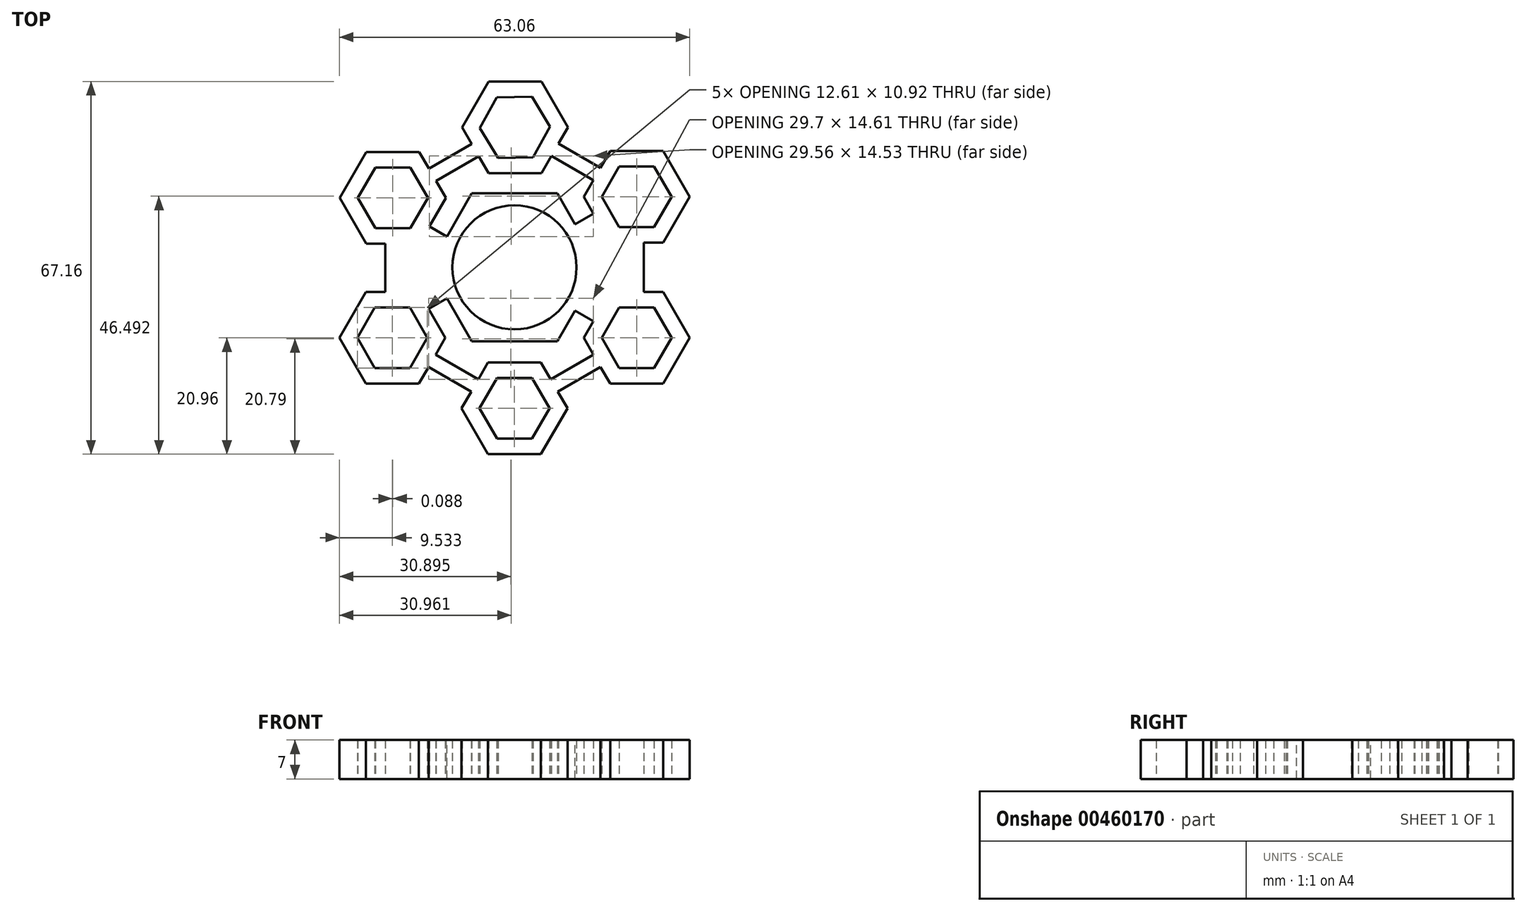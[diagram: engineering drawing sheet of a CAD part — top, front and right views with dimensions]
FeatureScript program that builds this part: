
annotation { "Feature Type Name" : "Feature", "Feature Type Description" : "" }
export const myFeature = defineFeature(function(context is Context, id is Id, definition is map)
    precondition{}
    {
        {
            var Q0;
            Q0=qCreatedBy(makeId("Top.planeOp"),FACE);
            var sketch = newSketch(context, id + "F0", { "sketchPlane" : qUnion([Q0])});
            skCircle(sketch, "E0", {"center": v(0, 0) * mm, "radius": 10.95 * mm});
            skCircle(sketch, "E1.cCircle", {"center": v(0, 0) * mm, "radius": 12.7 * mm, "construction": true});
            skLineSegment(sketch, "E1.0", {"start": v(-7.33, 12.7) * mm, "end": v(7.33, 12.7) * mm});
            skLineSegment(sketch, "E1.1", {"start": v(7.33, 12.7) * mm, "end": v(14.66, 0) * mm});
            skLineSegment(sketch, "E1.2", {"start": v(14.66, 0) * mm, "end": v(7.33, -12.7) * mm});
            skLineSegment(sketch, "E1.3", {"start": v(7.33, -12.7) * mm, "end": v(-7.33, -12.7) * mm});
            skLineSegment(sketch, "E1.4", {"start": v(-7.33, -12.7) * mm, "end": v(-14.66, 0) * mm});
            skLineSegment(sketch, "E1.5", {"start": v(-14.66, 0) * mm, "end": v(-7.33, 12.7) * mm});
            skPoint(sketch, "E1.0.midPoint", {"position": v(0, 12.7) * mm});
            skPoint(sketch, "E2.endSnap0", {"position": v(0, -12.7) * mm});
            skCircle(sketch, "E3.cCircle", {"center": v(0.09, 25.25) * mm, "radius": 5.46 * mm, "construction": true});
            skLineSegment(sketch, "E3.0", {"start": v(3.36, 19.86) * mm, "end": v(-2.94, 19.72) * mm});
            skLineSegment(sketch, "E3.1", {"start": v(-2.94, 19.72) * mm, "end": v(-6.22, 25.1) * mm});
            skLineSegment(sketch, "E3.2", {"start": v(-6.22, 25.1) * mm, "end": v(-3.18, 30.64) * mm});
            skLineSegment(sketch, "E3.3", {"start": v(-3.18, 30.64) * mm, "end": v(3.12, 30.78) * mm});
            skLineSegment(sketch, "E3.4", {"start": v(3.12, 30.78) * mm, "end": v(6.4, 25.39) * mm});
            skLineSegment(sketch, "E3.5", {"start": v(6.4, 25.39) * mm, "end": v(3.36, 19.86) * mm});
            skPoint(sketch, "E3.0.midPoint", {"position": v(0.2, 19.79) * mm});
            skCircle(sketch, "E4.cCircle", {"center": v(22, 12.7) * mm, "radius": 5.46 * mm, "construction": true});
            skLineSegment(sketch, "E4.0", {"start": v(18.84, 7.24) * mm, "end": v(15.7, 12.7) * mm});
            skLineSegment(sketch, "E4.1", {"start": v(15.7, 12.7) * mm, "end": v(18.84, 18.16) * mm});
            skLineSegment(sketch, "E4.2", {"start": v(18.84, 18.16) * mm, "end": v(25.15, 18.16) * mm});
            skLineSegment(sketch, "E4.3", {"start": v(25.15, 18.16) * mm, "end": v(28.3, 12.7) * mm});
            skLineSegment(sketch, "E4.4", {"start": v(28.3, 12.7) * mm, "end": v(25.15, 7.24) * mm});
            skLineSegment(sketch, "E4.5", {"start": v(25.15, 7.24) * mm, "end": v(18.84, 7.24) * mm});
            skPoint(sketch, "E4.0.midPoint", {"position": v(17.27, 9.97) * mm});
            skCircle(sketch, "E5.cCircle", {"center": v(22, -12.7) * mm, "radius": 5.46 * mm, "construction": true});
            skLineSegment(sketch, "E5.0", {"start": v(15.7, -12.7) * mm, "end": v(18.84, -7.24) * mm});
            skLineSegment(sketch, "E5.1", {"start": v(18.84, -7.24) * mm, "end": v(25.15, -7.24) * mm});
            skLineSegment(sketch, "E5.2", {"start": v(25.15, -7.24) * mm, "end": v(28.3, -12.7) * mm});
            skLineSegment(sketch, "E5.3", {"start": v(28.3, -12.7) * mm, "end": v(25.15, -18.16) * mm});
            skLineSegment(sketch, "E5.4", {"start": v(25.15, -18.16) * mm, "end": v(18.84, -18.16) * mm});
            skLineSegment(sketch, "E5.5", {"start": v(18.84, -18.16) * mm, "end": v(15.7, -12.7) * mm});
            skPoint(sketch, "E5.0.midPoint", {"position": v(17.27, -9.97) * mm});
            skCircle(sketch, "E6.cCircle", {"center": v(0, -25.4) * mm, "radius": 5.46 * mm, "construction": true});
            skLineSegment(sketch, "E6.0", {"start": v(-3.15, -19.94) * mm, "end": v(3.15, -19.94) * mm});
            skLineSegment(sketch, "E6.1", {"start": v(3.15, -19.94) * mm, "end": v(6.3, -25.4) * mm});
            skLineSegment(sketch, "E6.2", {"start": v(6.3, -25.4) * mm, "end": v(3.15, -30.86) * mm});
            skLineSegment(sketch, "E6.3", {"start": v(3.15, -30.86) * mm, "end": v(-3.15, -30.86) * mm});
            skLineSegment(sketch, "E6.4", {"start": v(-3.15, -30.86) * mm, "end": v(-6.3, -25.4) * mm});
            skLineSegment(sketch, "E6.5", {"start": v(-6.3, -25.4) * mm, "end": v(-3.15, -19.94) * mm});
            skPoint(sketch, "E6.0.midPoint", {"position": v(0, -19.94) * mm});
            skCircle(sketch, "E7.cCircle", {"center": v(-22, -12.7) * mm, "radius": 5.46 * mm, "construction": true});
            skLineSegment(sketch, "E7.0", {"start": v(-18.84, -7.24) * mm, "end": v(-15.7, -12.7) * mm});
            skLineSegment(sketch, "E7.1", {"start": v(-15.7, -12.7) * mm, "end": v(-18.84, -18.16) * mm});
            skLineSegment(sketch, "E7.2", {"start": v(-18.84, -18.16) * mm, "end": v(-25.15, -18.16) * mm});
            skLineSegment(sketch, "E7.3", {"start": v(-25.15, -18.16) * mm, "end": v(-28.3, -12.7) * mm});
            skLineSegment(sketch, "E7.4", {"start": v(-28.3, -12.7) * mm, "end": v(-25.15, -7.24) * mm});
            skLineSegment(sketch, "E7.5", {"start": v(-25.15, -7.24) * mm, "end": v(-18.84, -7.24) * mm});
            skPoint(sketch, "E7.0.midPoint", {"position": v(-17.27, -9.97) * mm});
            skCircle(sketch, "E8.cCircle", {"center": v(-21.9, 12.55) * mm, "radius": 5.46 * mm, "construction": true});
            skLineSegment(sketch, "E8.0", {"start": v(-15.6, 12.55) * mm, "end": v(-18.76, 7.09) * mm});
            skLineSegment(sketch, "E8.1", {"start": v(-18.76, 7.09) * mm, "end": v(-25.06, 7.09) * mm});
            skLineSegment(sketch, "E8.2", {"start": v(-25.06, 7.09) * mm, "end": v(-28.21, 12.55) * mm});
            skLineSegment(sketch, "E8.3", {"start": v(-28.21, 12.55) * mm, "end": v(-25.06, 18) * mm});
            skLineSegment(sketch, "E8.4", {"start": v(-25.06, 18) * mm, "end": v(-18.76, 18) * mm});
            skLineSegment(sketch, "E8.5", {"start": v(-18.76, 18) * mm, "end": v(-15.6, 12.55) * mm});
            skPoint(sketch, "E8.0.midPoint", {"position": v(-17.18, 9.82) * mm});
            skCircle(sketch, "E9.cCircle", {"center": v(-21.9, 12.55) * mm, "radius": 8.26 * mm, "construction": true});
            skLineSegment(sketch, "E9.0", {"start": v(-12.38, 12.55) * mm, "end": v(-17.14, 4.3) * mm});
            skLineSegment(sketch, "E9.1", {"start": v(-17.14, 4.3) * mm, "end": v(-26.67, 4.3) * mm});
            skLineSegment(sketch, "E9.2", {"start": v(-26.67, 4.3) * mm, "end": v(-31.44, 12.55) * mm});
            skLineSegment(sketch, "E9.3", {"start": v(-31.44, 12.55) * mm, "end": v(-26.67, 20.8) * mm});
            skLineSegment(sketch, "E9.4", {"start": v(-26.67, 20.8) * mm, "end": v(-17.14, 20.8) * mm});
            skLineSegment(sketch, "E9.5", {"start": v(-17.14, 20.8) * mm, "end": v(-12.38, 12.55) * mm});
            skPoint(sketch, "E9.0.midPoint", {"position": v(-14.76, 8.42) * mm});
            skCircle(sketch, "E10.cCircle", {"center": v(0.09, 25.25) * mm, "radius": 8.26 * mm, "construction": true});
            skLineSegment(sketch, "E10.0", {"start": v(4.85, 17) * mm, "end": v(-4.68, 17) * mm});
            skLineSegment(sketch, "E10.1", {"start": v(-4.68, 17) * mm, "end": v(-9.44, 25.25) * mm});
            skLineSegment(sketch, "E10.2", {"start": v(-9.44, 25.25) * mm, "end": v(-4.68, 33.5) * mm});
            skLineSegment(sketch, "E10.3", {"start": v(-4.68, 33.5) * mm, "end": v(4.85, 33.5) * mm});
            skLineSegment(sketch, "E10.4", {"start": v(4.85, 33.5) * mm, "end": v(9.62, 25.25) * mm});
            skLineSegment(sketch, "E10.5", {"start": v(9.62, 25.25) * mm, "end": v(4.85, 17) * mm});
            skPoint(sketch, "E10.0.midPoint", {"position": v(0.09, 17) * mm});
            skCircle(sketch, "E11.cCircle", {"center": v(22, 12.7) * mm, "radius": 8.26 * mm, "construction": true});
            skLineSegment(sketch, "E11.0", {"start": v(17.23, 4.45) * mm, "end": v(12.46, 12.7) * mm});
            skLineSegment(sketch, "E11.1", {"start": v(12.46, 12.7) * mm, "end": v(17.23, 20.96) * mm});
            skLineSegment(sketch, "E11.2", {"start": v(17.23, 20.96) * mm, "end": v(26.76, 20.96) * mm});
            skLineSegment(sketch, "E11.3", {"start": v(26.76, 20.96) * mm, "end": v(31.53, 12.7) * mm});
            skLineSegment(sketch, "E11.4", {"start": v(31.53, 12.7) * mm, "end": v(26.76, 4.45) * mm});
            skLineSegment(sketch, "E11.5", {"start": v(26.76, 4.45) * mm, "end": v(17.23, 4.45) * mm});
            skPoint(sketch, "E11.0.midPoint", {"position": v(14.85, 8.57) * mm});
            skCircle(sketch, "E12.cCircle", {"center": v(22, -12.7) * mm, "radius": 8.26 * mm, "construction": true});
            skLineSegment(sketch, "E12.0", {"start": v(12.46, -12.7) * mm, "end": v(17.23, -4.44) * mm});
            skLineSegment(sketch, "E12.1", {"start": v(17.23, -4.45) * mm, "end": v(26.76, -4.44) * mm});
            skLineSegment(sketch, "E12.2", {"start": v(26.76, -4.44) * mm, "end": v(31.53, -12.7) * mm});
            skLineSegment(sketch, "E12.3", {"start": v(31.53, -12.7) * mm, "end": v(26.76, -20.96) * mm});
            skLineSegment(sketch, "E12.4", {"start": v(26.76, -20.96) * mm, "end": v(17.23, -20.96) * mm});
            skLineSegment(sketch, "E12.5", {"start": v(17.23, -20.96) * mm, "end": v(12.46, -12.7) * mm});
            skPoint(sketch, "E12.0.midPoint", {"position": v(14.85, -8.57) * mm});
            skCircle(sketch, "E13.cCircle", {"center": v(0, -25.4) * mm, "radius": 8.26 * mm, "construction": true});
            skLineSegment(sketch, "E13.0", {"start": v(-4.77, -17.14) * mm, "end": v(4.77, -17.14) * mm});
            skLineSegment(sketch, "E13.1", {"start": v(4.77, -17.15) * mm, "end": v(9.53, -25.4) * mm});
            skLineSegment(sketch, "E13.2", {"start": v(9.53, -25.4) * mm, "end": v(4.77, -33.65) * mm});
            skLineSegment(sketch, "E13.3", {"start": v(4.77, -33.65) * mm, "end": v(-4.77, -33.66) * mm});
            skLineSegment(sketch, "E13.4", {"start": v(-4.77, -33.66) * mm, "end": v(-9.53, -25.4) * mm});
            skLineSegment(sketch, "E13.5", {"start": v(-9.53, -25.4) * mm, "end": v(-4.77, -17.15) * mm});
            skPoint(sketch, "E13.0.midPoint", {"position": v(0, -17.14) * mm});
            skCircle(sketch, "E14.cCircle", {"center": v(-22, -12.7) * mm, "radius": 8.26 * mm, "construction": true});
            skLineSegment(sketch, "E14.0", {"start": v(-17.23, -4.45) * mm, "end": v(-12.46, -12.7) * mm});
            skLineSegment(sketch, "E14.1", {"start": v(-12.46, -12.7) * mm, "end": v(-17.23, -20.96) * mm});
            skLineSegment(sketch, "E14.2", {"start": v(-17.23, -20.96) * mm, "end": v(-26.76, -20.96) * mm});
            skLineSegment(sketch, "E14.3", {"start": v(-26.76, -20.96) * mm, "end": v(-31.53, -12.7) * mm});
            skLineSegment(sketch, "E14.4", {"start": v(-31.53, -12.7) * mm, "end": v(-26.76, -4.45) * mm});
            skLineSegment(sketch, "E14.5", {"start": v(-26.76, -4.45) * mm, "end": v(-17.23, -4.45) * mm});
            skPoint(sketch, "E14.0.midPoint", {"position": v(-14.85, -8.57) * mm});
            skLineSegment(sketch, "E15", {"start": v(-6.43, 20.02) * mm, "end": v(-14.12, 15.57) * mm});
            skLineSegment(sketch, "E16", {"start": v(-14.21, 15.73) * mm, "end": v(-15.4, 17.77) * mm});
            skLineSegment(sketch, "E17", {"start": v(-15.4, 17.77) * mm, "end": v(-7.7, 22.22) * mm});
            skLineSegment(sketch, "E18", {"start": v(-23.27, 4.3) * mm, "end": v(-23.27, -4.45) * mm});
            skLineSegment(sketch, "E19", {"start": v(-23.27, -4.45) * mm, "end": v(-20.73, -4.45) * mm});
            skLineSegment(sketch, "E20", {"start": v(-20.73, -4.45) * mm, "end": v(-20.73, 4.3) * mm});
            skLineSegment(sketch, "E21", {"start": v(-15.48, -17.93) * mm, "end": v(-7.78, -22.37) * mm});
            skLineSegment(sketch, "E22", {"start": v(-7.78, -22.37) * mm, "end": v(-6.51, -20.17) * mm});
            skLineSegment(sketch, "E23", {"start": v(-6.51, -20.17) * mm, "end": v(-14.21, -15.73) * mm});
            skLineSegment(sketch, "E24", {"start": v(6.51, -20.17) * mm, "end": v(14.21, -15.73) * mm});
            skLineSegment(sketch, "E25", {"start": v(14.21, -15.73) * mm, "end": v(15.48, -17.93) * mm});
            skLineSegment(sketch, "E26", {"start": v(15.48, -17.93) * mm, "end": v(7.7, -22.42) * mm});
            skLineSegment(sketch, "E27", {"start": v(20.73, -4.45) * mm, "end": v(20.73, 4.45) * mm});
            skLineSegment(sketch, "E28", {"start": v(20.73, 4.45) * mm, "end": v(23.27, 4.45) * mm});
            skLineSegment(sketch, "E29", {"start": v(23.27, 4.45) * mm, "end": v(23.27, -4.54) * mm});
            skLineSegment(sketch, "E30", {"start": v(14.21, 15.73) * mm, "end": v(6.65, 20.1) * mm});
            skLineSegment(sketch, "E31", {"start": v(6.65, 20.1) * mm, "end": v(7.92, 22.3) * mm});
            skLineSegment(sketch, "E32", {"start": v(7.92, 22.3) * mm, "end": v(15.48, 17.93) * mm});
            skLineSegment(sketch, "E33.bottom", {"start": v(-1.27, -12.7) * mm, "end": v(1.27, -12.7) * mm});
            skLineSegment(sketch, "E33.top", {"start": v(-1.27, -17.14) * mm, "end": v(1.27, -17.14) * mm});
            skLineSegment(sketch, "E34.bottom", {"start": v(1.27, 12.7) * mm, "end": v(-1.27, 12.7) * mm});
            skLineSegment(sketch, "E34.top", {"start": v(1.27, 17) * mm, "end": v(-1.27, 17) * mm});
            skLineSegment(sketch, "E35", {"start": v(14.21, 9.67) * mm, "end": v(10.3, 7.42) * mm});
            skLineSegment(sketch, "E36", {"start": v(10.3, 7.42) * mm, "end": v(11.63, 5.25) * mm});
            skLineSegment(sketch, "E37", {"start": v(11.63, 5.25) * mm, "end": v(15.48, 7.47) * mm});
            skLineSegment(sketch, "E38", {"start": v(15.48, -7.47) * mm, "end": v(11.58, -5.22) * mm});
            skLineSegment(sketch, "E39", {"start": v(11.58, -5.22) * mm, "end": v(10.36, -7.45) * mm});
            skLineSegment(sketch, "E40", {"start": v(10.36, -7.45) * mm, "end": v(14.21, -9.67) * mm});
            skLineSegment(sketch, "E41", {"start": v(-10.36, -7.45) * mm, "end": v(-14.21, -9.67) * mm});
            skLineSegment(sketch, "E42", {"start": v(-14.21, -9.67) * mm, "end": v(-15.48, -7.47) * mm});
            skLineSegment(sketch, "E43", {"start": v(-15.48, -7.47) * mm, "end": v(-11.63, -5.25) * mm});
            skLineSegment(sketch, "E44", {"start": v(-11.63, 5.25) * mm, "end": v(-15.35, 7.4) * mm});
            skLineSegment(sketch, "E45", {"start": v(-15.35, 7.4) * mm, "end": v(-14.08, 9.6) * mm});
            skLineSegment(sketch, "E46", {"start": v(-14.08, 9.6) * mm, "end": v(-10.36, 7.45) * mm});
            skLineSegment(sketch, "E47", {"start": v(-11.63, 5.25) * mm, "end": v(-10.36, 7.45) * mm});
            skLineSegment(sketch, "E48", {"start": v(-14.08, 9.6) * mm, "end": v(-15.35, 7.4) * mm});
            skLineSegment(sketch, "E49", {"start": v(15.48, 7.47) * mm, "end": v(14.21, 9.67) * mm});
            skLineSegment(sketch, "E50", {"start": v(-11.63, -5.25) * mm, "end": v(-15.48, -7.47) * mm});
            skLineSegment(sketch, "E51", {"start": v(-15.48, -7.47) * mm, "end": v(-14.21, -9.67) * mm});
            skLineSegment(sketch, "E52", {"start": v(-14.21, -9.67) * mm, "end": v(-10.36, -7.45) * mm});
            skLineSegment(sketch, "E53", {"start": v(-10.36, -7.45) * mm, "end": v(-11.63, -5.25) * mm});
            skCircle(sketch, "E54", {"center": v(0, 0) * mm, "radius": 11.08 * mm});
            skCircle(sketch, "E55", {"center": v(0, 0) * mm, "radius": 11.07 * mm});
            skSolve(sketch);
        }
        {
            var Q0;
            Q0=qSketchRegion(id+"F0",true);
            var Q1;
            Q1=makeQuery(id+"F0.imprint","IMPRINT",FACE,{"disambiguationData":[TD([[makeQuery(id+"F0.imprint","IMPRINT",EDGE,{"derivedFrom":sQuery(id+"F0.wireOp",EDGE,"E34.bottom")}),-1.0]])]});
            var Q2;
            Q2=makeQuery(id+"F0.imprint","IMPRINT",FACE,{"disambiguationData":[TD([[makeQuery(id+"F0.imprint","IMPRINT",EDGE,{"derivedFrom":sQuery(id+"F0.wireOp",EDGE,"E50")}),1.0]])]});
            var Q3;
            Q3=makeQuery(id+"F0.imprint","IMPRINT",FACE,{"disambiguationData":[TD([[makeQuery(id+"F0.imprint","IMPRINT",EDGE,{"derivedFrom":sQuery(id+"F0.wireOp",EDGE,"E33.bottom")}),-1.0]])]});
            var Q4;
            {var subQ0=sQuery(id+"F0.wireOp",EDGE,"E40");Q4=makeQuery(id+"F0.imprint","IMPRINT",FACE,{"disambiguationData":[TD([[makeQuery(id+"F0.imprint","IMPRINT",EDGE,{"derivedFrom":subQ0}),1.0]])]});}
            var Q5;
            {var subQ0=sQuery(id+"F0.wireOp",EDGE,"E37");Q5=makeQuery(id+"F0.imprint","IMPRINT",FACE,{"disambiguationData":[TD([[makeQuery(id+"F0.imprint","IMPRINT",EDGE,{"derivedFrom":subQ0}),1.0]])]});}
            var Q6;
            Q6=makeQuery(id+"F0.imprint","IMPRINT",FACE,{"disambiguationData":[TD([[makeQuery(id+"F0.imprint","IMPRINT",EDGE,{"derivedFrom":sQuery(id+"F0.wireOp",EDGE,"E46")}),-1.0]])]});
            var Q7;
            {var subQ3=sQuery(id+"F0.wireOp",EDGE,"E27");Q7=makeQuery(id+"F0.imprint","IMPRINT",FACE,{"disambiguationData":[TD([[makeQuery(id+"F0.imprint","IMPRINT",EDGE,{"derivedFrom":subQ3}),1.0]])]});}
            var Q8;
            {var subQ7=sQuery(id+"F0.wireOp",EDGE,"E20");Q8=makeQuery(id+"F0.imprint","IMPRINT",FACE,{"disambiguationData":[TD([[makeQuery(id+"F0.imprint","IMPRINT",EDGE,{"derivedFrom":subQ7}),-1.0]])]});}
            extrude(context, id + "F1", {"entities" : qUnion([Q0, Q1, Q2, Q3, Q4, Q5, Q6, Q7, Q8]), "depth" : 7 * mm});
        }
        {
            var Q0;
            Q0=qCreatedBy(makeId("Top.planeOp"),FACE);
            var sketch = newSketch(context, id + "F2", { "sketchPlane" : qUnion([Q0])});
            skCircle(sketch, "E56", {"center": v(0, 0) * mm, "radius": 11.18 * mm});
            skCircle(sketch, "E57.cCircle", {"center": v(0, 0) * mm, "radius": 13.34 * mm, "construction": true});
            skLineSegment(sketch, "E57.0", {"start": v(-7.7, 13.33) * mm, "end": v(7.7, 13.34) * mm});
            skLineSegment(sketch, "E57.1", {"start": v(7.7, 13.34) * mm, "end": v(15.4, 0) * mm});
            skLineSegment(sketch, "E57.2", {"start": v(15.4, 0) * mm, "end": v(7.7, -13.33) * mm});
            skLineSegment(sketch, "E57.3", {"start": v(7.7, -13.33) * mm, "end": v(-7.7, -13.34) * mm});
            skLineSegment(sketch, "E57.4", {"start": v(-7.7, -13.34) * mm, "end": v(-15.4, 0) * mm});
            skLineSegment(sketch, "E57.5", {"start": v(-15.4, 0) * mm, "end": v(-7.7, 13.33) * mm});
            skPoint(sketch, "E57.0.midPoint", {"position": v(0, 13.33) * mm});
            skSolve(sketch);
        }
        {
            var Q0;
            Q0=qSketchRegion(id+"F2",true);
            extrude(context, id + "F3", {"entities" : qUnion([Q0]), "operationType" : NewBodyOperationType.ADD, "depth" : 7 * mm});
        }
    });
